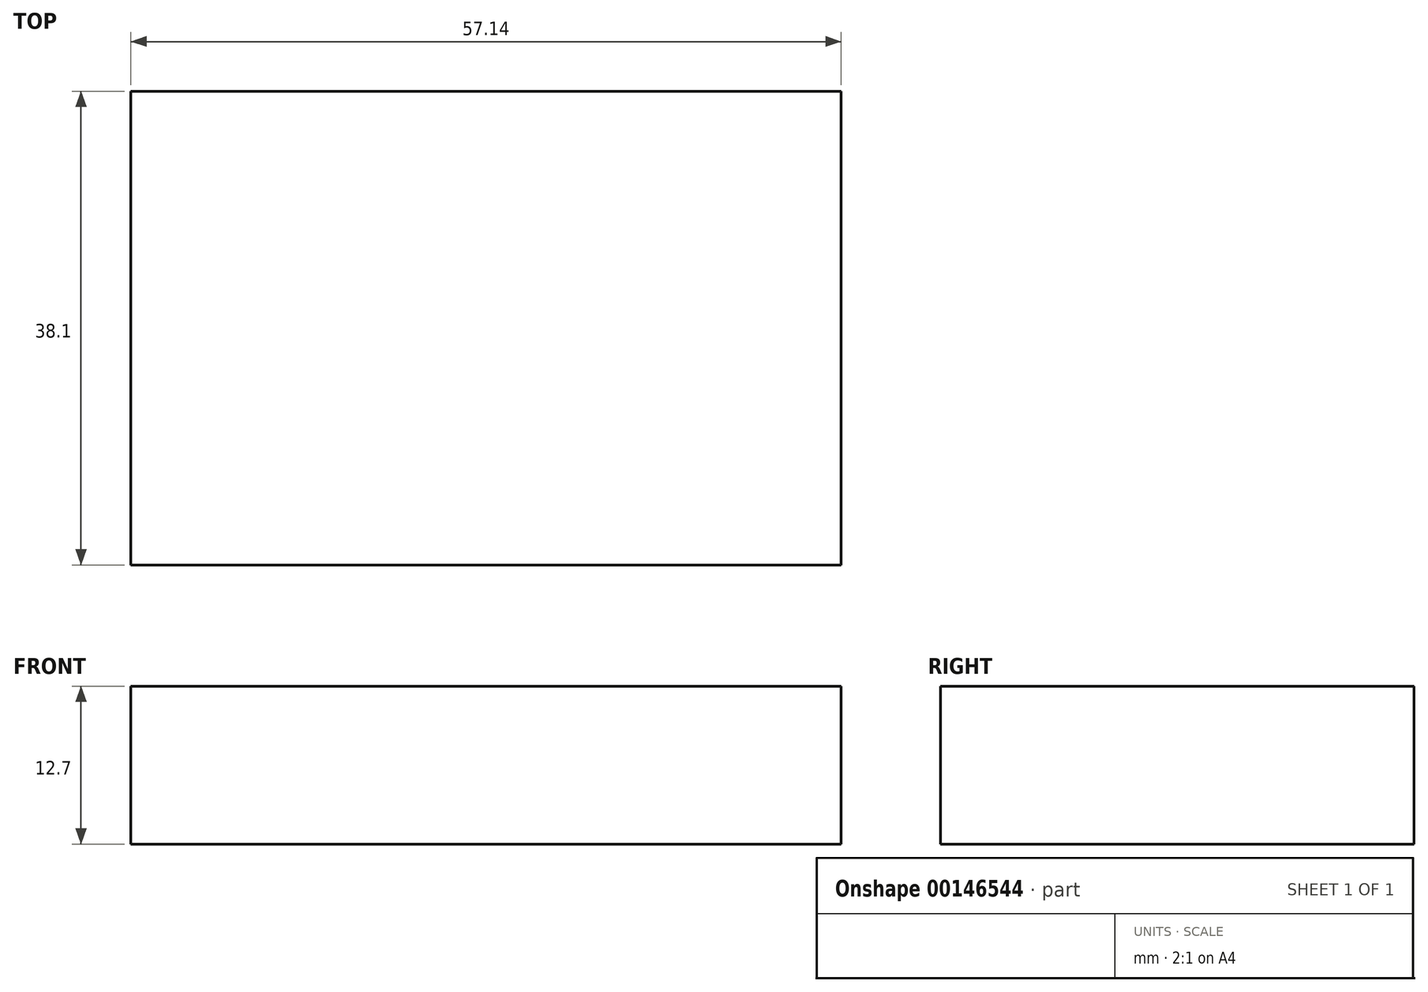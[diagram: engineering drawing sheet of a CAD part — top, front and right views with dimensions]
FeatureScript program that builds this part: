
annotation { "Feature Type Name" : "Feature", "Feature Type Description" : "" }
export const myFeature = defineFeature(function(context is Context, id is Id, definition is map)
    precondition{}
    {
        {
            var Q0;
            Q0=qCreatedBy(makeId("Top.planeOp"),FACE);
            var sketch = newSketch(context, id + "F0", { "sketchPlane" : qUnion([Q0])});
            skLineSegment(sketch, "E0.bottom", {"start": v(28.58, 19.05) * mm, "end": v(-28.57, 19.05) * mm});
            skLineSegment(sketch, "E0.top", {"start": v(28.57, -19.05) * mm, "end": v(-28.58, -19.05) * mm});
            skLineSegment(sketch, "E0.left", {"start": v(28.58, 19.05) * mm, "end": v(28.57, -19.05) * mm});
            skLineSegment(sketch, "E0.right", {"start": v(-28.57, 19.05) * mm, "end": v(-28.58, -19.05) * mm});
            skPoint(sketch, "E0.middle", {"position": v(0, 0) * mm});
            skSolve(sketch);
        }
        {
            var Q0;
            Q0 = qSketchRegion(id + "F0", true);
            extrude(context, id + "F1", {"entities" : qUnion([Q0]), "depth" : 12.7 * mm});
        }
    });
